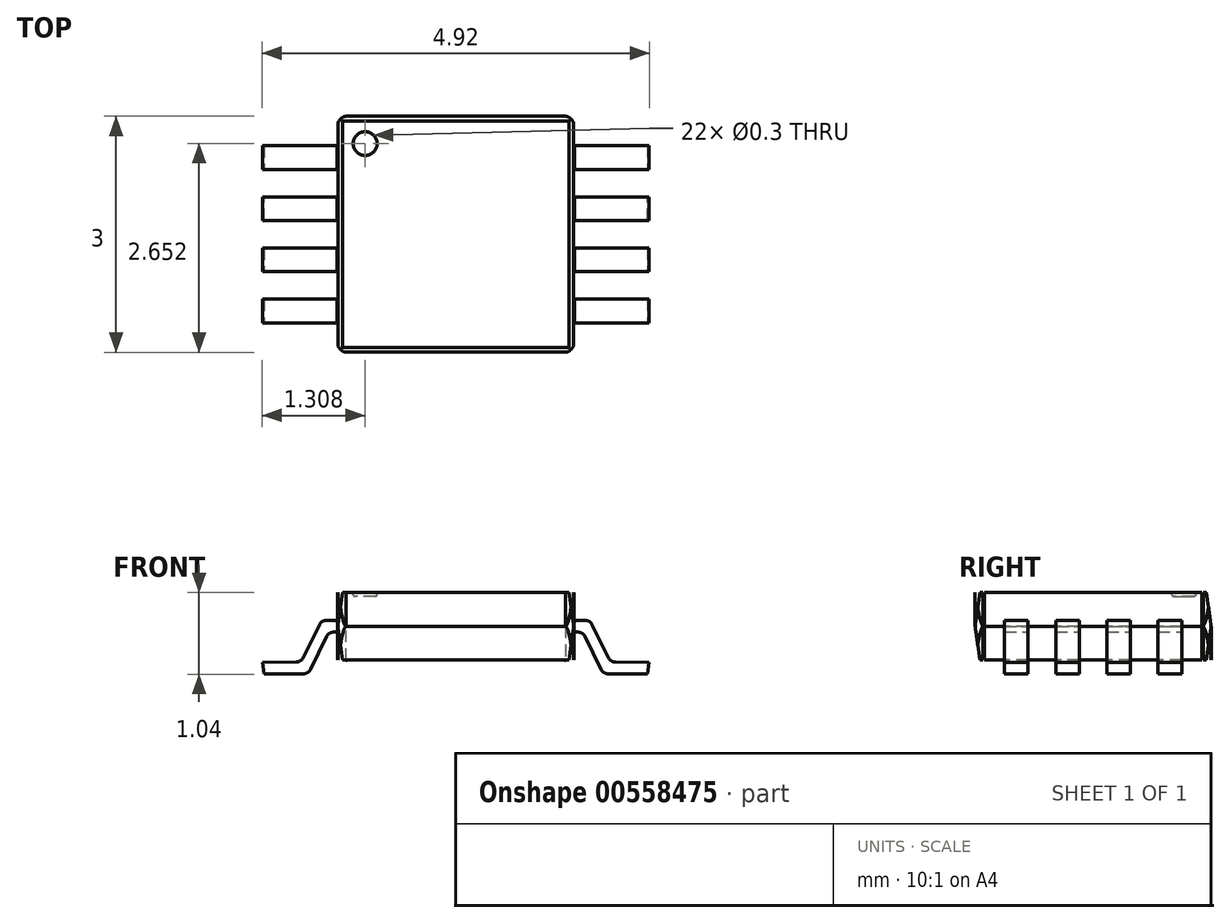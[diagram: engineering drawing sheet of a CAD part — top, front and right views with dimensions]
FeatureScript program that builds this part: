
annotation { "Feature Type Name" : "Feature", "Feature Type Description" : "" }
export const myFeature = defineFeature(function(context is Context, id is Id, definition is map)
    precondition{}
    {
        {
            var Q0;
            Q0=qCreatedBy(makeId("Top.planeOp"),FACE);
            var sketch = newSketch(context, id + "F0", { "sketchPlane" : qUnion([Q0])});
            skLineSegment(sketch, "E0.bottom", {"start": v(-1.5, 1.5) * mm, "end": v(1.5, 1.5) * mm});
            skLineSegment(sketch, "E0.top", {"start": v(-1.5, -1.5) * mm, "end": v(1.5, -1.5) * mm});
            skLineSegment(sketch, "E0.left", {"start": v(-1.5, 1.5) * mm, "end": v(-1.5, -1.5) * mm});
            skLineSegment(sketch, "E0.right", {"start": v(1.5, 1.5) * mm, "end": v(1.5, -1.5) * mm});
            skPoint(sketch, "E0.middle", {"position": v(0, 0) * mm});
            skSolve(sketch);
        }
        {
            var Q0;
            Q0=makeQuery(id+"F0.imprint","IMPRINT",FACE,{"disambiguationData":[TD([[makeQuery(id+"F0.imprint","IMPRINT",EDGE,{"derivedFrom":sQuery(id+"F0.wireOp",EDGE,"E0.bottom")}),-1.0]])]});
            extrude(context, id + "F1", {"entities" : qUnion([Q0]), "endBound" : BoundingType.SYMMETRIC, "depth" : 0.86 * mm, "offsetDistance" : 25 * mm});
        }
        {
            var Q0;
            Q0=makeQuery(id+"F1.opExtrude","SWEPT_EDGE",EDGE,{"disambiguationData":[OSD([sQuery(id+"F0.wireOp",EDGE,"E0.bottom"),sQuery(id+"F0.wireOp",EDGE,"E0.left")])]});
            var Q1;
            Q1=makeQuery(id+"F1.opExtrude","SWEPT_EDGE",EDGE,{"disambiguationData":[OSD([sQuery(id+"F0.wireOp",EDGE,"E0.top"),sQuery(id+"F0.wireOp",EDGE,"E0.left")])]});
            var Q2;
            Q2=makeQuery(id+"F1.opExtrude","SWEPT_EDGE",EDGE,{"disambiguationData":[OSD([sQuery(id+"F0.wireOp",EDGE,"E0.top"),sQuery(id+"F0.wireOp",EDGE,"E0.right")])]});
            var Q3;
            Q3=makeQuery(id+"F1.opExtrude","SWEPT_EDGE",EDGE,{"disambiguationData":[OSD([sQuery(id+"F0.wireOp",EDGE,"E0.bottom"),sQuery(id+"F0.wireOp",EDGE,"E0.right")])]});
            fillet(context, id + "F2", {"entities" : qUnion([Q0, Q1, Q2, Q3]), "radius" : 0.12 * mm, "tangentPropagation" : true, "allowEdgeOverflow" : false});
        }
        {
            var Q0;
            Q0=qCreatedBy(makeId("Front.planeOp"),FACE);
            var sketch = newSketch(context, id + "F3", { "sketchPlane" : qUnion([Q0])});
            skLineSegment(sketch, "E1", {"start": v(1.44, 0.43) * mm, "end": v(1.5, 0) * mm});
            skLineSegment(sketch, "E2", {"start": v(1.5, 0) * mm, "end": v(1.5, 0.43) * mm});
            skLineSegment(sketch, "E3", {"start": v(1.5, 0.43) * mm, "end": v(1.44, 0.43) * mm});
            skLineSegment(sketch, "E4.MirrorCS", {"start": v(1.44, -0.43) * mm, "end": v(1.5, 0) * mm});
            skLineSegment(sketch, "E5.MirrorCS", {"start": v(1.5, 0) * mm, "end": v(1.5, -0.43) * mm});
            skLineSegment(sketch, "E6.MirrorCS", {"start": v(1.5, -0.43) * mm, "end": v(1.44, -0.43) * mm});
            skLineSegment(sketch, "E7.MirrorCS", {"start": v(-1.44, 0.43) * mm, "end": v(-1.5, 0) * mm});
            skLineSegment(sketch, "E8.MirrorCS", {"start": v(-1.5, 0) * mm, "end": v(-1.5, 0.43) * mm});
            skLineSegment(sketch, "E9.MirrorCS", {"start": v(-1.5, 0.43) * mm, "end": v(-1.44, 0.43) * mm});
            skLineSegment(sketch, "E10.MirrorCS", {"start": v(-1.44, -0.43) * mm, "end": v(-1.5, 0) * mm});
            skLineSegment(sketch, "E11.MirrorCS", {"start": v(-1.5, 0) * mm, "end": v(-1.5, -0.43) * mm});
            skLineSegment(sketch, "E12.MirrorCS", {"start": v(-1.5, -0.43) * mm, "end": v(-1.44, -0.43) * mm});
            skSolve(sketch);
        }
        {
            var Q0;
            Q0 = qSketchRegion(id + "F3", true);
            extrude(context, id + "F4", {"entities" : qUnion([Q0]), "operationType" : NewBodyOperationType.REMOVE, "endBound" : BoundingType.SYMMETRIC, "oppositeDirection" : true, "depth" : 3 * mm, "offsetDistance" : 25 * mm});
        }
        {
            var Q0;
            Q0=qCreatedBy(makeId("Right.planeOp"),FACE);
            var sketch = newSketch(context, id + "F5", { "sketchPlane" : qUnion([Q0])});
            skLineSegment(sketch, "E13", {"start": v(-1.5, 0) * mm, "end": v(-1.5, 0.43) * mm});
            skLineSegment(sketch, "E14", {"start": v(-1.5, 0.43) * mm, "end": v(-1.44, 0.43) * mm});
            skLineSegment(sketch, "E15", {"start": v(-1.44, 0.43) * mm, "end": v(-1.5, 0) * mm});
            skLineSegment(sketch, "E16.MirrorCS", {"start": v(-1.44, -0.43) * mm, "end": v(-1.5, 0) * mm});
            skLineSegment(sketch, "E17.MirrorCS", {"start": v(-1.5, 0) * mm, "end": v(-1.5, -0.43) * mm});
            skLineSegment(sketch, "E18.MirrorCS", {"start": v(-1.5, -0.43) * mm, "end": v(-1.44, -0.43) * mm});
            skLineSegment(sketch, "E19.MirrorCS", {"start": v(1.44, 0.43) * mm, "end": v(1.5, 0) * mm});
            skLineSegment(sketch, "E20.MirrorCS", {"start": v(1.5, 0.43) * mm, "end": v(1.44, 0.43) * mm});
            skLineSegment(sketch, "E21.MirrorCS", {"start": v(1.5, 0) * mm, "end": v(1.5, 0.43) * mm});
            skLineSegment(sketch, "E22.MirrorCS", {"start": v(1.44, -0.43) * mm, "end": v(1.5, 0) * mm});
            skLineSegment(sketch, "E23.MirrorCS", {"start": v(1.5, 0) * mm, "end": v(1.5, -0.43) * mm});
            skLineSegment(sketch, "E24.MirrorCS", {"start": v(1.5, -0.43) * mm, "end": v(1.44, -0.43) * mm});
            skSolve(sketch);
        }
        {
            var Q0;
            Q0 = qSketchRegion(id + "F5", true);
            extrude(context, id + "F6", {"entities" : qUnion([Q0]), "operationType" : NewBodyOperationType.REMOVE, "endBound" : BoundingType.SYMMETRIC, "oppositeDirection" : true, "depth" : 3 * mm, "offsetDistance" : 25 * mm});
        }
        {
            var Q0;
            Q0=qCreatedBy(makeId("Front.planeOp"),FACE);
            var sketch = newSketch(context, id + "F7", { "sketchPlane" : qUnion([Q0])});
            skLineSegment(sketch, "E25", {"start": v(1.92, -0.53) * mm, "end": v(2.45, -0.53) * mm});
            skLineSegment(sketch, "E26", {"start": v(1.92, -0.53) * mm, "end": v(1.66, 0) * mm});
            skLineSegment(sketch, "E27", {"start": v(1.66, 0) * mm, "end": v(1.5, 0) * mm});
            skLineSegment(sketch, "E28.MirrorCS", {"start": v(-1.66, 0) * mm, "end": v(-1.5, 0) * mm});
            skLineSegment(sketch, "E29.MirrorCS", {"start": v(-1.92, -0.53) * mm, "end": v(-1.66, 0) * mm});
            skLineSegment(sketch, "E30.MirrorCS", {"start": v(-1.92, -0.53) * mm, "end": v(-2.45, -0.53) * mm});
            skSolve(sketch);
        }
        {
            var Q0;
            Q0=makeQuery(id+"F4.boolean.opBoolean","COPY",FACE,{"derivedFrom":makeQuery(id+"F4.opExtrude","SWEPT_FACE",FACE,{"disambiguationData":[OSD([sQuery(id+"F3.wireOp",EDGE,"E10.MirrorCS")])]})});
            var sketch = newSketch(context, id + "F8", { "sketchPlane" : qUnion([Q0])});
            skLineSegment(sketch, "E31.bottom", {"start": v(-0.18, 0.28) * mm, "end": v(-0.47, 0.28) * mm});
            skLineSegment(sketch, "E31.top", {"start": v(-0.17, 0.13) * mm, "end": v(-0.47, 0.13) * mm});
            skLineSegment(sketch, "E31.left", {"start": v(-0.18, 0.28) * mm, "end": v(-0.17, 0.13) * mm});
            skLineSegment(sketch, "E31.right", {"start": v(-0.47, 0.28) * mm, "end": v(-0.47, 0.13) * mm});
            skLineSegment(sketch, "E32.bottom", {"start": v(0.17, 0.28) * mm, "end": v(0.48, 0.28) * mm});
            skLineSegment(sketch, "E32.top", {"start": v(0.17, 0.13) * mm, "end": v(0.48, 0.13) * mm});
            skLineSegment(sketch, "E32.left", {"start": v(0.17, 0.28) * mm, "end": v(0.17, 0.13) * mm});
            skLineSegment(sketch, "E32.right", {"start": v(0.48, 0.28) * mm, "end": v(0.48, 0.13) * mm});
            skLineSegment(sketch, "E33.bottom", {"start": v(0.83, 0.28) * mm, "end": v(1.13, 0.28) * mm});
            skLineSegment(sketch, "E33.top", {"start": v(0.83, 0.13) * mm, "end": v(1.13, 0.13) * mm});
            skLineSegment(sketch, "E33.left", {"start": v(0.83, 0.28) * mm, "end": v(0.83, 0.13) * mm});
            skLineSegment(sketch, "E33.right", {"start": v(1.13, 0.28) * mm, "end": v(1.13, 0.13) * mm});
            skLineSegment(sketch, "E34.bottom", {"start": v(-1.12, 0.28) * mm, "end": v(-0.82, 0.28) * mm});
            skLineSegment(sketch, "E34.top", {"start": v(-1.12, 0.13) * mm, "end": v(-0.82, 0.13) * mm});
            skLineSegment(sketch, "E34.left", {"start": v(-1.12, 0.28) * mm, "end": v(-1.12, 0.13) * mm});
            skLineSegment(sketch, "E34.right", {"start": v(-0.82, 0.28) * mm, "end": v(-0.82, 0.13) * mm});
            skSolve(sketch);
        }
        {
            var Q0;
            {var subQ0=sQuery(id+"F8.wireOp",EDGE,"E31.top");Q0=makeQuery(id+"F8.imprint","IMPRINT",FACE,{"disambiguationData":[TD([[makeQuery(id+"F8.imprint","IMPRINT",EDGE,{"derivedFrom":subQ0}),-1.0]])]});}
            var Q1;
            {var subQ0=sQuery(id+"F8.wireOp",EDGE,"E31.bottom");Q1=makeQuery(id+"F8.imprint","IMPRINT",FACE,{"disambiguationData":[TD([[makeQuery(id+"F8.imprint","IMPRINT",EDGE,{"derivedFrom":subQ0}),1.0]])]});}
            var Q2;
            {var subQ0=sQuery(id+"F8.wireOp",EDGE,"E34.top");Q2=makeQuery(id+"F8.imprint","IMPRINT",FACE,{"disambiguationData":[TD([[makeQuery(id+"F8.imprint","IMPRINT",EDGE,{"derivedFrom":subQ0}),1.0]])]});}
            var Q3;
            {var subQ0=sQuery(id+"F8.wireOp",EDGE,"E34.bottom");Q3=makeQuery(id+"F8.imprint","IMPRINT",FACE,{"disambiguationData":[TD([[makeQuery(id+"F8.imprint","IMPRINT",EDGE,{"derivedFrom":subQ0}),-1.0]])]});}
            var Q4;
            {var subQ0=sQuery(id+"F8.wireOp",EDGE,"E32.top");Q4=makeQuery(id+"F8.imprint","IMPRINT",FACE,{"disambiguationData":[TD([[makeQuery(id+"F8.imprint","IMPRINT",EDGE,{"derivedFrom":subQ0}),1.0]])]});}
            var Q5;
            {var subQ0=sQuery(id+"F8.wireOp",EDGE,"E32.bottom");Q5=makeQuery(id+"F8.imprint","IMPRINT",FACE,{"disambiguationData":[TD([[makeQuery(id+"F8.imprint","IMPRINT",EDGE,{"derivedFrom":subQ0}),-1.0]])]});}
            var Q6;
            {var subQ0=sQuery(id+"F8.wireOp",EDGE,"E33.top");Q6=makeQuery(id+"F8.imprint","IMPRINT",FACE,{"disambiguationData":[TD([[makeQuery(id+"F8.imprint","IMPRINT",EDGE,{"derivedFrom":subQ0}),1.0]])]});}
            var Q7;
            {var subQ0=sQuery(id+"F8.wireOp",EDGE,"E33.bottom");Q7=makeQuery(id+"F8.imprint","IMPRINT",FACE,{"disambiguationData":[TD([[makeQuery(id+"F8.imprint","IMPRINT",EDGE,{"derivedFrom":subQ0}),-1.0]])]});}
            var Q8;
            Q8=sQuery(id+"F7.wireOp",EDGE,"E28.MirrorCS");
            var Q9;
            Q9=sQuery(id+"F7.wireOp",EDGE,"E29.MirrorCS");
            var Q10;
            Q10=sQuery(id+"F7.wireOp",EDGE,"E30.MirrorCS");
            sweep(context, id + "F9", {"profiles" : qUnion([Q0, Q1, Q2, Q3, Q4, Q5, Q6, Q7]), "path" : qUnion([Q8, Q9, Q10])});
        }
        {
            var Q0;
            Q0=makeQuery(id+"F1.opExtrude","SWEPT_BODY",BODY,{"disambiguationData":[OSD([sQuery(id+"F0.wireOp",EDGE,"E0.bottom"),sQuery(id+"F0.wireOp",EDGE,"E0.top"),sQuery(id+"F0.wireOp",EDGE,"E0.left"),sQuery(id+"F0.wireOp",EDGE,"E0.right")])]});
            var Q1;
            Q1=qCreatedBy(makeId("Right.planeOp"),FACE);
            mirror(context, id + "F10", {"operationType" : NewBodyOperationType.ADD, "entities" : qUnion([Q0]), "mirrorPlane" : qUnion([Q1])});
        }
        {
            var Q0;
            Q0=makeQuery(id+"F10.opPattern","COPY",EDGE,{"derivedFrom":makeQuery(id+"F9.opSweep","MID_CAP_EDGE",EDGE,{"disambiguationData":[OSD([sQuery(id+"F7.wireOp",VERTEX,"E29.MirrorCS.end"),sQuery(id+"F8.wireOp",EDGE,"E33.bottom")])],"capPos":1.0}),"instanceName":"1"});
            var Q1;
            Q1=makeQuery(id+"F10.opPattern","COPY",EDGE,{"derivedFrom":makeQuery(id+"F9.opSweep","MID_CAP_EDGE",EDGE,{"disambiguationData":[OSD([sQuery(id+"F7.wireOp",VERTEX,"E29.MirrorCS.end"),sQuery(id+"F8.wireOp",EDGE,"E32.bottom")])],"capPos":1.0}),"instanceName":"1"});
            var Q2;
            Q2=makeQuery(id+"F10.opPattern","COPY",EDGE,{"derivedFrom":makeQuery(id+"F9.opSweep","MID_CAP_EDGE",EDGE,{"disambiguationData":[OSD([sQuery(id+"F7.wireOp",VERTEX,"E30.MirrorCS.start"),sQuery(id+"F8.wireOp",EDGE,"E32.bottom")])],"capPos":2.0}),"instanceName":"1"});
            var Q3;
            Q3=makeQuery(id+"F10.opPattern","COPY",EDGE,{"derivedFrom":makeQuery(id+"F9.opSweep","MID_CAP_EDGE",EDGE,{"disambiguationData":[OSD([sQuery(id+"F7.wireOp",VERTEX,"E30.MirrorCS.start"),sQuery(id+"F8.wireOp",EDGE,"E33.bottom")])],"capPos":2.0}),"instanceName":"1"});
            var Q4;
            Q4=makeQuery(id+"F10.opPattern","COPY",EDGE,{"derivedFrom":makeQuery(id+"F9.opSweep","MID_CAP_EDGE",EDGE,{"disambiguationData":[OSD([sQuery(id+"F7.wireOp",VERTEX,"E29.MirrorCS.end"),sQuery(id+"F8.wireOp",EDGE,"E31.bottom")])],"capPos":1.0}),"instanceName":"1"});
            var Q5;
            Q5=makeQuery(id+"F10.opPattern","COPY",EDGE,{"derivedFrom":makeQuery(id+"F9.opSweep","MID_CAP_EDGE",EDGE,{"disambiguationData":[OSD([sQuery(id+"F7.wireOp",VERTEX,"E30.MirrorCS.start"),sQuery(id+"F8.wireOp",EDGE,"E31.bottom")])],"capPos":2.0}),"instanceName":"1"});
            var Q6;
            Q6=makeQuery(id+"F10.opPattern","COPY",EDGE,{"derivedFrom":makeQuery(id+"F9.opSweep","MID_CAP_EDGE",EDGE,{"disambiguationData":[OSD([sQuery(id+"F7.wireOp",VERTEX,"E29.MirrorCS.end"),sQuery(id+"F8.wireOp",EDGE,"E34.bottom")])],"capPos":1.0}),"instanceName":"1"});
            var Q7;
            Q7=makeQuery(id+"F10.opPattern","COPY",EDGE,{"derivedFrom":makeQuery(id+"F9.opSweep","MID_CAP_EDGE",EDGE,{"disambiguationData":[OSD([sQuery(id+"F7.wireOp",VERTEX,"E30.MirrorCS.start"),sQuery(id+"F8.wireOp",EDGE,"E34.bottom")])],"capPos":2.0}),"instanceName":"1"});
            var Q8;
            Q8=makeQuery(id+"F9.opSweep","MID_CAP_EDGE",EDGE,{"disambiguationData":[OSD([sQuery(id+"F7.wireOp",VERTEX,"E29.MirrorCS.end"),sQuery(id+"F8.wireOp",EDGE,"E33.bottom")])],"capPos":1.0});
            var Q9;
            Q9=makeQuery(id+"F9.opSweep","MID_CAP_EDGE",EDGE,{"disambiguationData":[OSD([sQuery(id+"F7.wireOp",VERTEX,"E30.MirrorCS.start"),sQuery(id+"F8.wireOp",EDGE,"E33.bottom")])],"capPos":2.0});
            var Q10;
            Q10=makeQuery(id+"F9.opSweep","MID_CAP_EDGE",EDGE,{"disambiguationData":[OSD([sQuery(id+"F7.wireOp",VERTEX,"E29.MirrorCS.end"),sQuery(id+"F8.wireOp",EDGE,"E32.bottom")])],"capPos":1.0});
            var Q11;
            Q11=makeQuery(id+"F9.opSweep","MID_CAP_EDGE",EDGE,{"disambiguationData":[OSD([sQuery(id+"F7.wireOp",VERTEX,"E30.MirrorCS.start"),sQuery(id+"F8.wireOp",EDGE,"E32.bottom")])],"capPos":2.0});
            var Q12;
            Q12=makeQuery(id+"F9.opSweep","MID_CAP_EDGE",EDGE,{"disambiguationData":[OSD([sQuery(id+"F7.wireOp",VERTEX,"E29.MirrorCS.end"),sQuery(id+"F8.wireOp",EDGE,"E31.bottom")])],"capPos":1.0});
            var Q13;
            Q13=makeQuery(id+"F9.opSweep","MID_CAP_EDGE",EDGE,{"disambiguationData":[OSD([sQuery(id+"F7.wireOp",VERTEX,"E30.MirrorCS.start"),sQuery(id+"F8.wireOp",EDGE,"E31.bottom")])],"capPos":2.0});
            var Q14;
            Q14=makeQuery(id+"F9.opSweep","MID_CAP_EDGE",EDGE,{"disambiguationData":[OSD([sQuery(id+"F7.wireOp",VERTEX,"E29.MirrorCS.end"),sQuery(id+"F8.wireOp",EDGE,"E34.bottom")])],"capPos":1.0});
            var Q15;
            Q15=makeQuery(id+"F9.opSweep","MID_CAP_EDGE",EDGE,{"disambiguationData":[OSD([sQuery(id+"F7.wireOp",VERTEX,"E30.MirrorCS.start"),sQuery(id+"F8.wireOp",EDGE,"E34.bottom")])],"capPos":2.0});
            var Q16;
            Q16=makeQuery(id+"F9.opSweep","MID_CAP_EDGE",EDGE,{"disambiguationData":[OSD([sQuery(id+"F7.wireOp",VERTEX,"E29.MirrorCS.end"),sQuery(id+"F8.wireOp",EDGE,"E34.top")])],"capPos":1.0});
            var Q17;
            Q17=makeQuery(id+"F9.opSweep","MID_CAP_EDGE",EDGE,{"disambiguationData":[OSD([sQuery(id+"F7.wireOp",VERTEX,"E30.MirrorCS.start"),sQuery(id+"F8.wireOp",EDGE,"E34.top")])],"capPos":2.0});
            var Q18;
            Q18=makeQuery(id+"F9.opSweep","MID_CAP_EDGE",EDGE,{"disambiguationData":[OSD([sQuery(id+"F7.wireOp",VERTEX,"E29.MirrorCS.end"),sQuery(id+"F8.wireOp",EDGE,"E31.top")])],"capPos":1.0});
            var Q19;
            Q19=makeQuery(id+"F9.opSweep","MID_CAP_EDGE",EDGE,{"disambiguationData":[OSD([sQuery(id+"F7.wireOp",VERTEX,"E30.MirrorCS.start"),sQuery(id+"F8.wireOp",EDGE,"E31.top")])],"capPos":2.0});
            var Q20;
            Q20=makeQuery(id+"F9.opSweep","MID_CAP_EDGE",EDGE,{"disambiguationData":[OSD([sQuery(id+"F7.wireOp",VERTEX,"E29.MirrorCS.end"),sQuery(id+"F8.wireOp",EDGE,"E32.top")])],"capPos":1.0});
            var Q21;
            Q21=makeQuery(id+"F9.opSweep","MID_CAP_EDGE",EDGE,{"disambiguationData":[OSD([sQuery(id+"F7.wireOp",VERTEX,"E30.MirrorCS.start"),sQuery(id+"F8.wireOp",EDGE,"E32.top")])],"capPos":2.0});
            var Q22;
            Q22=makeQuery(id+"F9.opSweep","MID_CAP_EDGE",EDGE,{"disambiguationData":[OSD([sQuery(id+"F7.wireOp",VERTEX,"E29.MirrorCS.end"),sQuery(id+"F8.wireOp",EDGE,"E33.top")])],"capPos":1.0});
            var Q23;
            Q23=makeQuery(id+"F9.opSweep","MID_CAP_EDGE",EDGE,{"disambiguationData":[OSD([sQuery(id+"F7.wireOp",VERTEX,"E30.MirrorCS.start"),sQuery(id+"F8.wireOp",EDGE,"E33.top")])],"capPos":2.0});
            var Q24;
            Q24=makeQuery(id+"F10.opPattern","COPY",EDGE,{"derivedFrom":makeQuery(id+"F9.opSweep","MID_CAP_EDGE",EDGE,{"disambiguationData":[OSD([sQuery(id+"F7.wireOp",VERTEX,"E29.MirrorCS.end"),sQuery(id+"F8.wireOp",EDGE,"E33.top")])],"capPos":1.0}),"instanceName":"1"});
            var Q25;
            Q25=makeQuery(id+"F10.opPattern","COPY",EDGE,{"derivedFrom":makeQuery(id+"F9.opSweep","MID_CAP_EDGE",EDGE,{"disambiguationData":[OSD([sQuery(id+"F7.wireOp",VERTEX,"E29.MirrorCS.end"),sQuery(id+"F8.wireOp",EDGE,"E32.top")])],"capPos":1.0}),"instanceName":"1"});
            var Q26;
            Q26=makeQuery(id+"F10.opPattern","COPY",EDGE,{"derivedFrom":makeQuery(id+"F9.opSweep","MID_CAP_EDGE",EDGE,{"disambiguationData":[OSD([sQuery(id+"F7.wireOp",VERTEX,"E29.MirrorCS.end"),sQuery(id+"F8.wireOp",EDGE,"E31.top")])],"capPos":1.0}),"instanceName":"1"});
            var Q27;
            Q27=makeQuery(id+"F10.opPattern","COPY",EDGE,{"derivedFrom":makeQuery(id+"F9.opSweep","MID_CAP_EDGE",EDGE,{"disambiguationData":[OSD([sQuery(id+"F7.wireOp",VERTEX,"E29.MirrorCS.end"),sQuery(id+"F8.wireOp",EDGE,"E34.top")])],"capPos":1.0}),"instanceName":"1"});
            var Q28;
            Q28=makeQuery(id+"F10.opPattern","COPY",EDGE,{"derivedFrom":makeQuery(id+"F9.opSweep","MID_CAP_EDGE",EDGE,{"disambiguationData":[OSD([sQuery(id+"F7.wireOp",VERTEX,"E30.MirrorCS.start"),sQuery(id+"F8.wireOp",EDGE,"E34.top")])],"capPos":2.0}),"instanceName":"1"});
            var Q29;
            Q29=makeQuery(id+"F10.opPattern","COPY",EDGE,{"derivedFrom":makeQuery(id+"F9.opSweep","MID_CAP_EDGE",EDGE,{"disambiguationData":[OSD([sQuery(id+"F7.wireOp",VERTEX,"E30.MirrorCS.start"),sQuery(id+"F8.wireOp",EDGE,"E31.top")])],"capPos":2.0}),"instanceName":"1"});
            var Q30;
            Q30=makeQuery(id+"F10.opPattern","COPY",EDGE,{"derivedFrom":makeQuery(id+"F9.opSweep","MID_CAP_EDGE",EDGE,{"disambiguationData":[OSD([sQuery(id+"F7.wireOp",VERTEX,"E30.MirrorCS.start"),sQuery(id+"F8.wireOp",EDGE,"E32.top")])],"capPos":2.0}),"instanceName":"1"});
            var Q31;
            Q31=makeQuery(id+"F10.opPattern","COPY",EDGE,{"derivedFrom":makeQuery(id+"F9.opSweep","MID_CAP_EDGE",EDGE,{"disambiguationData":[OSD([sQuery(id+"F7.wireOp",VERTEX,"E30.MirrorCS.start"),sQuery(id+"F8.wireOp",EDGE,"E33.top")])],"capPos":2.0}),"instanceName":"1"});
            fillet(context, id + "F11", {"entities" : qUnion([Q0, Q1, Q2, Q3, Q4, Q5, Q6, Q7, Q8, Q9, Q10, Q11, Q12, Q13, Q14, Q15, Q16, Q17, Q18, Q19, Q20, Q21, Q22, Q23, Q24, Q25, Q26, Q27, Q28, Q29, Q30, Q31]), "radius" : 0.1 * mm, "tangentPropagation" : true, "allowEdgeOverflow" : false});
        }
        {
            var Q0;
            Q0=makeQuery(id+"F1.opExtrude","CAP_FACE",FACE,{"disambiguationData":[OSD([sQuery(id+"F0.wireOp",EDGE,"E0.bottom"),sQuery(id+"F0.wireOp",EDGE,"E0.top"),sQuery(id+"F0.wireOp",EDGE,"E0.left"),sQuery(id+"F0.wireOp",EDGE,"E0.right")])],"isStart":false});
            var sketch = newSketch(context, id + "F12", { "sketchPlane" : qUnion([Q0])});
            skCircle(sketch, "E35", {"center": v(-1.15, 1.15) * mm, "radius": 0.15 * mm});
            skSolve(sketch);
        }
        {
            var Q0;
            Q0=makeQuery(id+"F12.imprint","IMPRINT",FACE,{"disambiguationData":[TD([[makeQuery(id+"F12.imprint","IMPRINT",EDGE,{"derivedFrom":sQuery(id+"F12.wireOp",EDGE,"E35")}),1.0]])]});
            extrude(context, id + "F13", {"entities" : qUnion([Q0]), "operationType" : NewBodyOperationType.REMOVE, "oppositeDirection" : true, "depth" : 0.05 * mm, "offsetDistance" : 25 * mm});
        }
        {
            var Q0;
            Q0=makeQuery(id+"F13.boolean.opBoolean","COPY",EDGE,{"derivedFrom":makeQuery(id+"F13.opExtrude","CAP_EDGE",EDGE,{"disambiguationData":[OSD([sQuery(id+"F12.wireOp",EDGE,"E35")])],"isStart":true})});
            var Q1;
            Q1=makeQuery(id+"F13.boolean.opBoolean","COPY",EDGE,{"derivedFrom":makeQuery(id+"F13.opExtrude","CAP_EDGE",EDGE,{"disambiguationData":[OSD([sQuery(id+"F12.wireOp",EDGE,"E35")])],"isStart":false})});
            fillet(context, id + "F14", {"entities" : qUnion([Q0, Q1]), "radius" : 0.02 * mm, "tangentPropagation" : true, "allowEdgeOverflow" : false});
        }
        {
            var Q0;
            Q0=makeQuery(id+"F9.opSweep","SWEPT_BODY",BODY,{"disambiguationData":[OSD([sQuery(id+"F7.wireOp",EDGE,"E30.MirrorCS"),sQuery(id+"F8.wireOp",EDGE,"E34.bottom"),sQuery(id+"F8.wireOp",EDGE,"E34.top"),sQuery(id+"F8.wireOp",EDGE,"E34.left"),sQuery(id+"F8.wireOp",EDGE,"E34.right")])]});
            var Q1;
            Q1=makeQuery(id+"F9.opSweep","SWEPT_BODY",BODY,{"disambiguationData":[OSD([sQuery(id+"F7.wireOp",EDGE,"E30.MirrorCS"),sQuery(id+"F8.wireOp",EDGE,"E31.bottom"),sQuery(id+"F8.wireOp",EDGE,"E31.top"),sQuery(id+"F8.wireOp",EDGE,"E31.left"),sQuery(id+"F8.wireOp",EDGE,"E31.right")])]});
            var Q2;
            Q2=makeQuery(id+"F9.opSweep","SWEPT_BODY",BODY,{"disambiguationData":[OSD([sQuery(id+"F7.wireOp",EDGE,"E30.MirrorCS"),sQuery(id+"F8.wireOp",EDGE,"E32.bottom"),sQuery(id+"F8.wireOp",EDGE,"E32.top"),sQuery(id+"F8.wireOp",EDGE,"E32.left"),sQuery(id+"F8.wireOp",EDGE,"E32.right")])]});
            var Q3;
            Q3=makeQuery(id+"F9.opSweep","SWEPT_BODY",BODY,{"disambiguationData":[OSD([sQuery(id+"F7.wireOp",EDGE,"E30.MirrorCS"),sQuery(id+"F8.wireOp",EDGE,"E33.bottom"),sQuery(id+"F8.wireOp",EDGE,"E33.top"),sQuery(id+"F8.wireOp",EDGE,"E33.left"),sQuery(id+"F8.wireOp",EDGE,"E33.right")])]});
            var Q4;
            Q4=qCreatedBy(makeId("Right.planeOp"),FACE);
            mirror(context, id + "F15", {"entities" : qUnion([Q0, Q1, Q2, Q3]), "mirrorPlane" : qUnion([Q4])});
        }
    });
